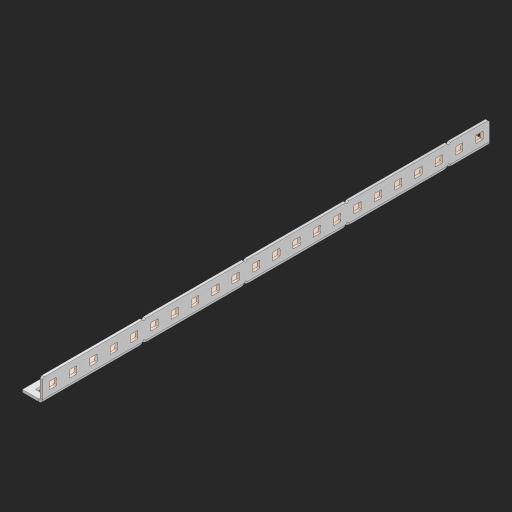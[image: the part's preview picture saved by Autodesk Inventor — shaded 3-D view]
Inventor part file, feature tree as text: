
AUTODESK INVENTOR PART (.ipt)
format: ipt  version: 2023 (Build 270158000, 158)  size: 811,008 bytes
history: native  units: in
note: dims shown in document units (in); Inventor stores cm internally (conversion verified against a paired STEP export)
features: other x49, extrude x43, sheet_metal_op x10, sketch x8, mirror x1, pattern_linear x1, chamfer x1
ambient origin geometry x8: Origin, YZ Plane, XZ Plane, XY Plane, X Axis, Y Axis, Z Axis, Center Point
bodies: Solid1 (feature_tree), Body (feature_tree)
feature tree (113):
  other  "Flange Pattern Plane"
  sheet_metal_op  "Flange Pattern"
  sheet_metal_op  "Body Pattern"
  other  "Arc Length"
  mirror  "Notch Mirror"
  pattern_linear  "Notch Pattern"  Spacing1=0.25in  [1 undecoded]
  chamfer  "End Chamfer"
  extrude  "Half Cut"  Depth=0.0625in
  sketch  "Sketch1"  dims[d0=1.5in]
  other  "Plate1"
  sketch  "Sketch2"  dims[d1=11.0in]
  other  "Plate2"
  sheet_metal_op  "Bend1"
  sheet_metal_op  "Corner1"
  sketch  "Sketch3"  dims[d2=0.0625in]
  other  "Flange Pattern Sketch"
  sketch  "Sketch7"  dims[d3=0.0625in]
  other  "Srf1"
  other  "Srf2"
  sketch  "Sketch8"  dims[d4=0.0312in]
  sketch  "Sketch9"  dims[d5=0.125in]
  other  "Srf91"
  sheet_metal_op  "Body Pattern Sketch"
  other  "Srf92"
  sketch  "Sketch13"  dims[d6=0.0625in]
  sketch  "Sketch14"  dims[d7=0.5in d8=90.0deg d9=0.0312in d10=0.25in d11=0.0625in d12=0.0625in d16=0.182in d17=0.02in d18=0.0625in d19=0.0in d20=0.25in d21=0.25in d46=0.172in d47=1.0in d48=0.0in d49=0.182in d50=0.02in d51=0.25in d52=0.25in d53=0.0625in d54=0.0in d55=0.172in d56=1.0in d57=0.0in d60=8.6614in d62=0.5in d63=0.3937in d65=0.5in d85=0.1473in d86=0.1782in d88=0.04in d89=0.0625in d90=0.0in d91=0.04in d92=0.0491in d95=2.5in d96=0.04in d97=0.25in d98=45.0deg d101=0.0in d102=2.497in d131=0.5in d132=8.6614in d134=0.5in d139=0.5in]
  other  "Srf856"
  other  "Srf1310"
  other  "Srf1311"
  other  "Srf1312"
  other  "Srf1376"
  other  "Srf1377"
  other  "Srf1728"
  other  "Srf1755"
  other  "Srf1878"
  other  "Srf1879"
  other  "Srf1880"
  other  "Srf1881"
  other  "Srf1882"
  other  "Srf1883"
  other  "Srf1884"
  other  "Srf1885"
  other  "Srf1886"
  other  "Srf1887"
  other  "Srf1888"
  other  "Srf1889"
  other  "Srf1890"
  other  "Srf1891"
  other  "Srf1892"
  other  "Srf1893"
  other  "Srf1942"
  other  "Srf1943"
  other  "Srf1944"
  other  "Srf1945"
  other  "Srf1946"
  other  "Srf1947"
  other  "Srf1948"
  other  "Srf1949"
  other  "Srf1950"
  other  "Srf1951"
  other  "Srf1952"
  other  "Srf1953"
  other  "Srf1954"
  other  "Srf1955"
  other  "Srf1956"
  other  "Srf1957"
  sheet_metal_op  "Flange Stamp"
  sheet_metal_op  "Flange Circle"
  sheet_metal_op  "Body Stamp"
  sheet_metal_op  "Body Circle"
  sheet_metal_op  "Notch"
  extrude  "ExtrusionSrf2"  Depth=0.0625in
  extrude  "ExtrusionSrf92"  Depth=0.5in
  extrude  "ExtrusionSrf856"  Depth=0.02in
  extrude  "ExtrusionSrf1310"  Depth=0.0625in
  extrude  "ExtrusionSrf1311"  TaperAngle=0.0deg  [1 undecoded]
  extrude  "ExtrusionSrf1312"  Depth=0.5in
  extrude  "ExtrusionSrf1376"  Depth=0.5in
  extrude  "ExtrusionSrf1377"  Depth=0.5in
  extrude  "ExtrusionSrf1728"  Depth=0.5in TaperAngle=0.0deg
  extrude  "ExtrusionSrf1755"  Depth=0.5in
  extrude  "ExtrusionSrf1878"  Depth=0.02in
  extrude  "ExtrusionSrf1879"  Depth=0.5in
  extrude  "ExtrusionSrf1880"  Depth=0.5in
  extrude  "ExtrusionSrf1881"  Depth=0.0625in
  extrude  "ExtrusionSrf1882"  TaperAngle=0.0deg  [1 undecoded]
  extrude  "ExtrusionSrf1883"  Depth=0.5in
  extrude  "ExtrusionSrf1884"  Depth=0.5in TaperAngle=0.0deg
  extrude  "ExtrusionSrf1885"  Depth=0.5in
  extrude  "ExtrusionSrf1886"  Depth=0.5in
  extrude  "ExtrusionSrf1887"  Depth=0.5in
  extrude  "ExtrusionSrf1888"  Depth=0.5in
  extrude  "ExtrusionSrf1889"  Depth=0.5in
  extrude  "ExtrusionSrf1890"  Depth=0.0625in
  extrude  "ExtrusionSrf1891"  TaperAngle=0.0deg  [1 undecoded]
  extrude  "ExtrusionSrf1892"  Depth=0.5in
  extrude  "ExtrusionSrf1893"  Depth=0.5in
  extrude  "ExtrusionSrf1942"  Depth=0.5in
  extrude  "ExtrusionSrf1943"  Depth=0.5in TaperAngle=45.0deg
  extrude  "ExtrusionSrf1944"  TaperAngle=0.0deg  [1 undecoded]
  extrude  "ExtrusionSrf1945"  Depth=0.5in
  extrude  "ExtrusionSrf1946"  Depth=0.5in
  extrude  "ExtrusionSrf1947"  Depth=0.5in
  extrude  "ExtrusionSrf1948"  Depth=0.5in
  extrude  "ExtrusionSrf1949"  Depth=0.5in
  extrude  "ExtrusionSrf1950"  [1 undecoded]
  extrude  "ExtrusionSrf1951"  [1 undecoded]
  extrude  "ExtrusionSrf1952"  [1 undecoded]
  extrude  "ExtrusionSrf1953"  [1 undecoded]
  extrude  "ExtrusionSrf1954"  [1 undecoded]
  extrude  "ExtrusionSrf1955"  [1 undecoded]
  extrude  "ExtrusionSrf1956"  [1 undecoded]
  extrude  "ExtrusionSrf1957"  [1 undecoded]
note: 13 required parameter values undecoded (feature->parameter linkage not recoverable at this tier; creation-order binding heuristic only, values carry confidence <= 0.55)
